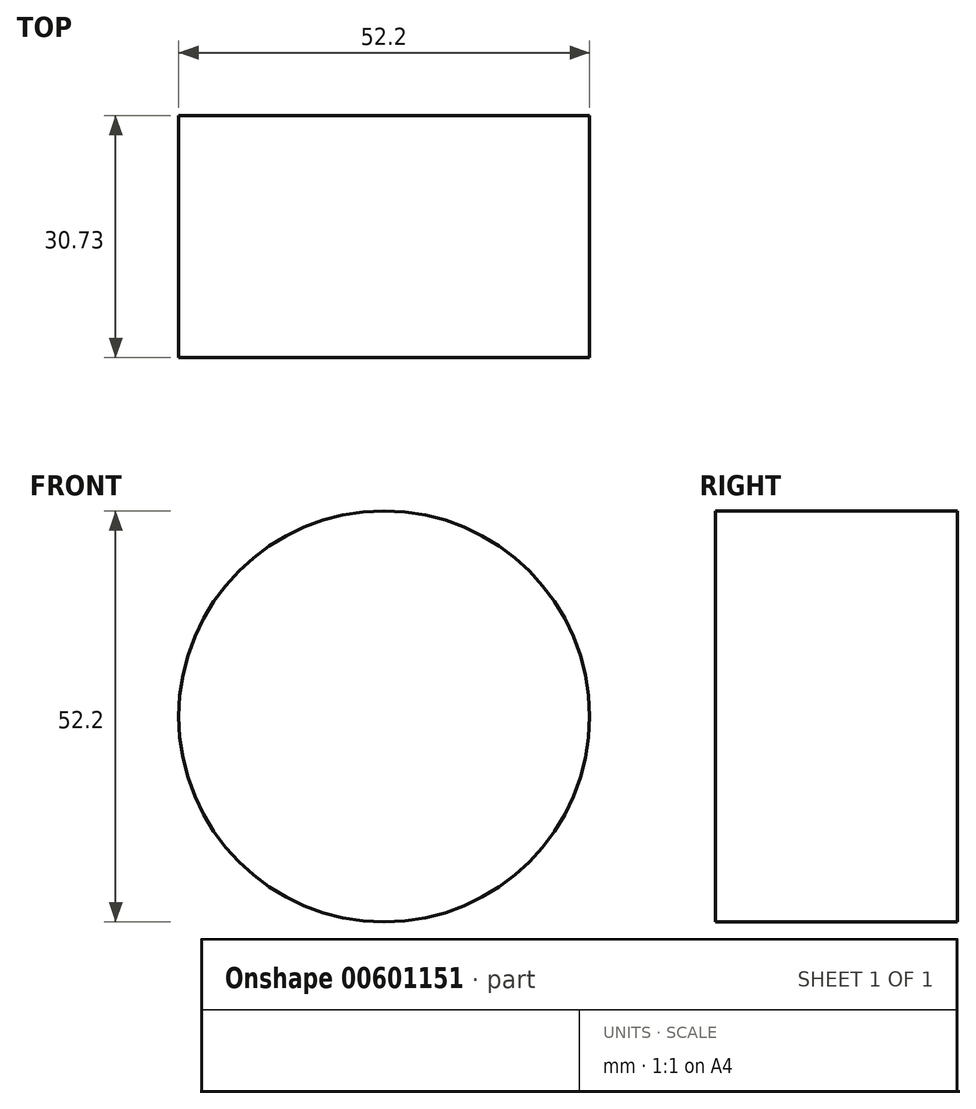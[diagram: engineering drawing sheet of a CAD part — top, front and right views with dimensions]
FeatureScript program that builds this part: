
annotation { "Feature Type Name" : "Feature", "Feature Type Description" : "" }
export const myFeature = defineFeature(function(context is Context, id is Id, definition is map)
    precondition{}
    {
        {
            var Q0;
            Q0=qCreatedBy(makeId("Front.planeOp"),FACE);
            var sketch = newSketch(context, id + "F0", { "sketchPlane" : qUnion([Q0])});
            skCircle(sketch, "E0", {"center": v(0, 0) * mm, "radius": 26.1 * mm});
            skSolve(sketch);
        }
        {
            var Q0;
            Q0 = qSketchRegion(id + "F0", true);
            extrude(context, id + "F1", {"entities" : qUnion([Q0]), "depth" : 30.73 * mm, "offsetDistance" : 25.4 * mm});
        }
    });
